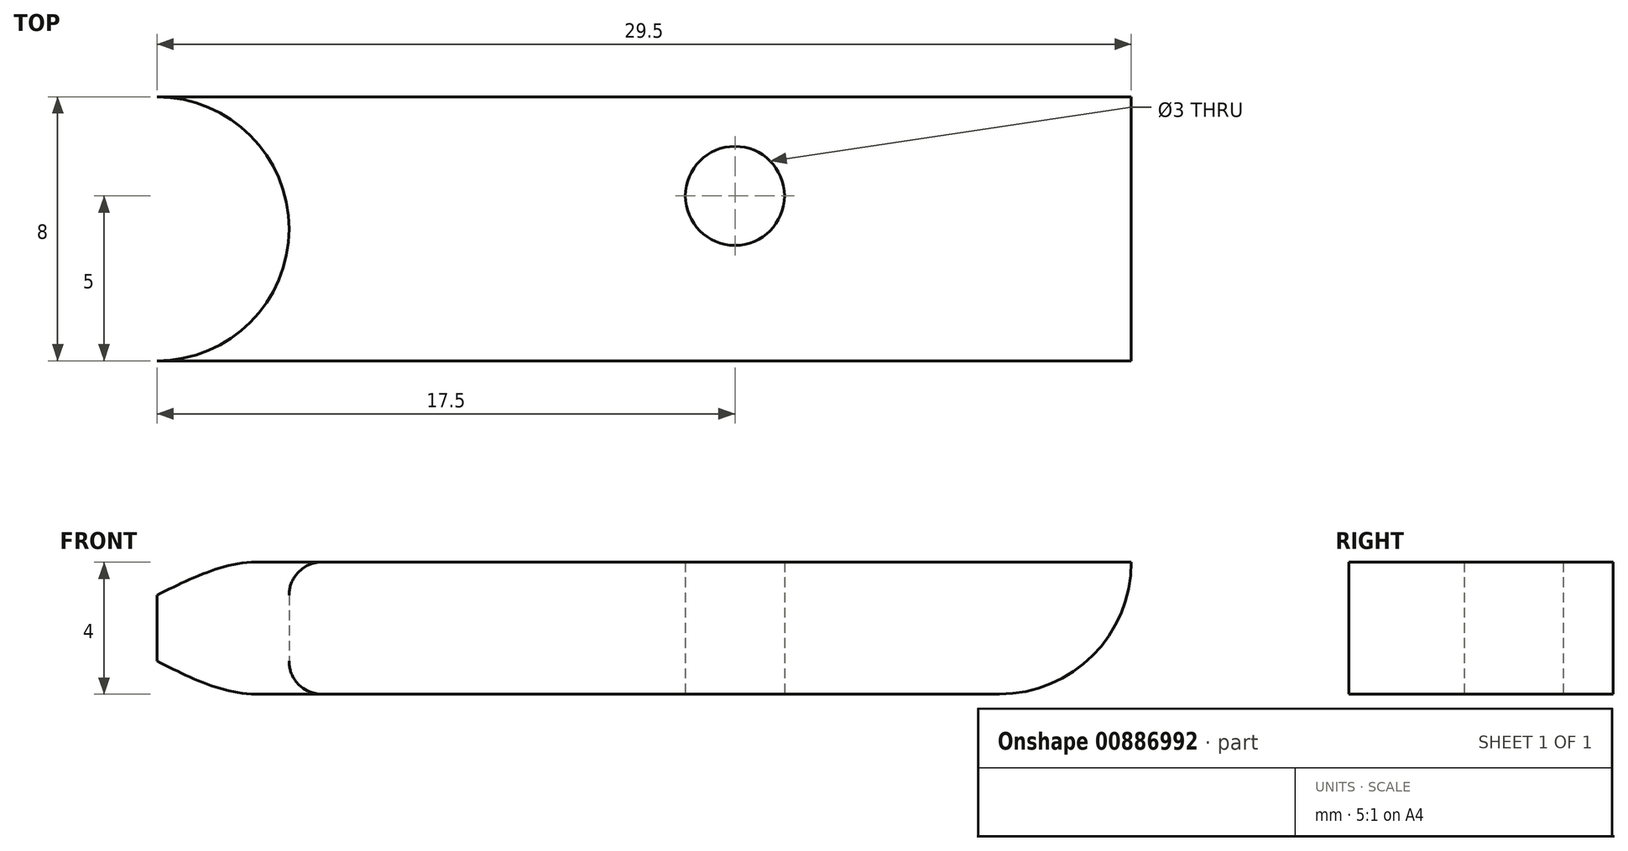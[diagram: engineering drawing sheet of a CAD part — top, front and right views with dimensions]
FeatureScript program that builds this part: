
annotation { "Feature Type Name" : "Feature", "Feature Type Description" : "" }
export const myFeature = defineFeature(function(context is Context, id is Id, definition is map)
    precondition{}
    {
        {
            var Q0;
            Q0=qCreatedBy(makeId("Top.planeOp"),FACE);
            var sketch = newSketch(context, id + "F0", { "sketchPlane" : qUnion([Q0])});
            skCircle(sketch, "E0", {"center": v(0, 4) * mm, "radius": 4 * mm});
            skCircle(sketch, "E1", {"center": v(17.5, 5) * mm, "radius": 1.5 * mm});
            skLineSegment(sketch, "E2", {"start": v(0, 8) * mm, "end": v(29.5, 8) * mm});
            skLineSegment(sketch, "E3", {"start": v(0, 0) * mm, "end": v(29.5, 0) * mm});
            skLineSegment(sketch, "E4", {"start": v(29.5, 8) * mm, "end": v(29.5, 0) * mm});
            skSolve(sketch);
        }
        {
            var Q0;
            Q0=makeQuery(id+"F0.imprint","IMPRINT",FACE,{"disambiguationData":[TD([[makeQuery(id+"F0.imprint","IMPRINT",EDGE,{"derivedFrom":sQuery(id+"F0.wireOp",EDGE,"E1")}),-1.0]])]});
            extrude(context, id + "F1", {"entities" : qUnion([Q0]), "depth" : 4 * mm, "offsetDistance" : 25 * mm});
        }
        {
            var Q0;
            Q0=makeQuery(id+"F1.opExtrude","CAP_EDGE",EDGE,{"disambiguationData":[OSD([sQuery(id+"F0.wireOp",EDGE,"E0")])],"isStart":true});
            var Q1;
            Q1=makeQuery(id+"F1.opExtrude","CAP_EDGE",EDGE,{"disambiguationData":[OSD([sQuery(id+"F0.wireOp",EDGE,"E0")])],"isStart":false});
            fillet(context, id + "F2", {"entities" : qUnion([Q0, Q1]), "radius" : 1 * mm, "tangentPropagation" : true, "allowEdgeOverflow" : false});
        }
        {
            var Q0;
            Q0=makeQuery(id+"F1.opExtrude","CAP_EDGE",EDGE,{"disambiguationData":[OSD([sQuery(id+"F0.wireOp",EDGE,"E4")])],"isStart":true});
            fillet(context, id + "F3", {"entities" : qUnion([Q0]), "radius" : 4 * mm, "tangentPropagation" : true, "allowEdgeOverflow" : false});
        }
    });
